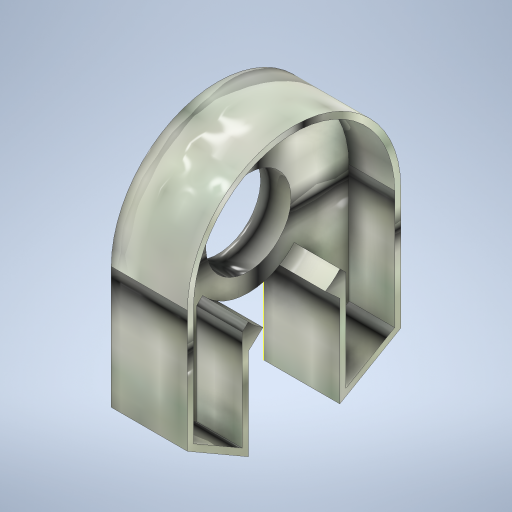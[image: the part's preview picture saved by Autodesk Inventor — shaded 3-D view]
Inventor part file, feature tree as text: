
AUTODESK INVENTOR PART (.ipt)
format: ipt  version: 2023 (Build 270158000, 158)  size: 637,952 bytes
history: native  units: mm
features: extrude x2, sketch x1
ambient origin geometry x8: Origin, YZ Plane, XZ Plane, XY Plane, X Axis, Y Axis, Z Axis, Center Point
bodies: Body1 (feature_tree)
feature tree (3):
  extrude  "Extrusion3"  Depth=15.0mm
  extrude  "Extrusion4"  Depth=2.0mm
  sketch  "Sketch2"  dims[d0=70.0mm d9=15.0mm d17=6.0mm d27=25.0mm d28=0.0mm d29=10.0mm d30=0.0mm d32=40.0mm d43=20.0mm d44=30.0deg d45=30.0mm d47=2.0mm d48=45.0deg d49=23.09157mm d50=1.306712mm d51=30.659518mm d52=29.0mm d54=2.990754mm d23=0.5mm d24=0.872665mm d25=0.5mm d26=0.872665mm]
